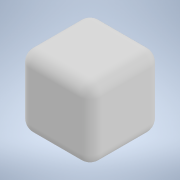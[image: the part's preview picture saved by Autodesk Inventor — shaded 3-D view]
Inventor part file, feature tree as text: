
AUTODESK INVENTOR PART (.ipt)
format: ipt  version: 2022 (Build 260153000, 153)  size: 122,368 bytes
history: native  units: mm
features: other x1, extrude x1, fillet x1, sketch x1
ambient origin geometry x8: Origin, YZ Plane, XZ Plane, XY Plane, X Axis, Y Axis, Z Axis, Center Point
bodies: Body1 (feature_tree)
feature tree (4):
  other  "Твердое тело1"
  extrude  "Выдавливание1"  Depth=10.5mm
  fillet  "Сопряжение1"  Radius=10.5mm
  sketch  "Эскиз1"
